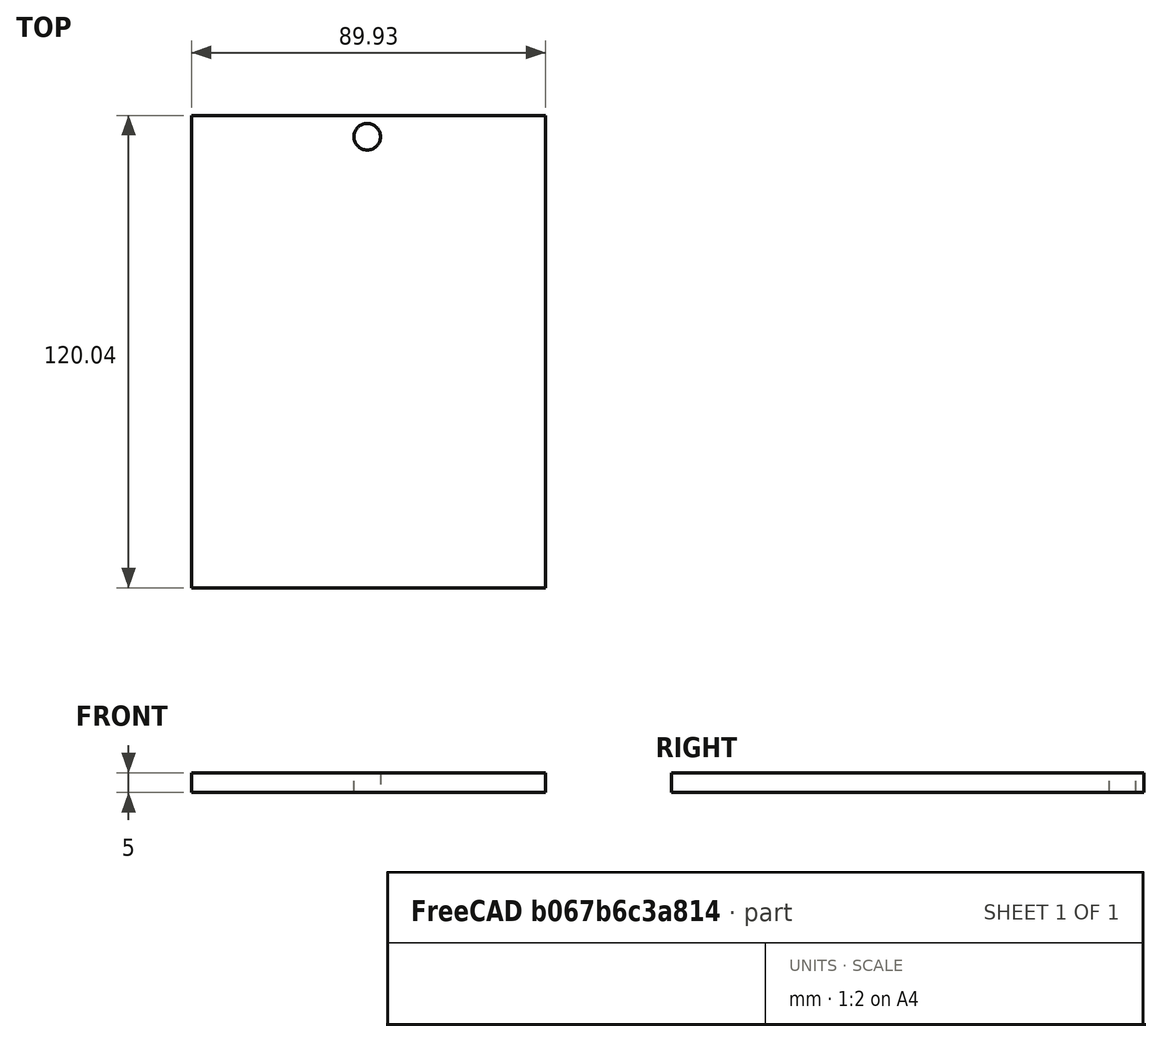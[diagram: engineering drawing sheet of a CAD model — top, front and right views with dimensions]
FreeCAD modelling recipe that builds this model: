
FCSTD DOCUMENT  (FreeCAD 0.14R3702 (Git))
Label: escarrilla
License: CC-BY 3.0
LicenseURL: http://creativecommons.org/licenses/by/3.0/
objects: Sketcher::SketchObject×2, Mesh::Feature×1, PartDesign::Pad×1, PartDesign::Pocket×1
note: 6 computed .brp shape members not serialized (recipe doc carries the construction recipe); baked Part::Feature solids carry a one-line shape summary decoded from their .brp

FEATURE [Mesh::Feature] escarrilla
  Placement = pos=(-64,-50,0) rot=(0,0,1;0rad)
FEATURE [Sketcher::SketchObject] Sketch001
  sketch-geometry (4):
    g0: LineSegment StartX=-9.69851 StartY=109.858 StartZ=0 EndX=80.2331 EndY=109.858 EndZ=0
    g1: LineSegment StartX=80.2331 StartY=109.858 StartZ=0 EndX=80.2331 EndY=-10.1794 EndZ=0
    g2: LineSegment StartX=80.2331 StartY=-10.1794 StartZ=0 EndX=-9.69851 EndY=-10.1794 EndZ=0
    g3: LineSegment StartX=-9.69851 StartY=-10.1794 StartZ=0 EndX=-9.69851 EndY=109.858 EndZ=0
  constraints (8):
    c: Coincident(g0,g1)
    c: Coincident(g1,g2)
    c: Coincident(g2,g3)
    c: Coincident(g3,g0)
    c: Horizontal(g0)
    c: Horizontal(g2)
    c: Vertical(g1)
    c: Vertical(g3)
FEATURE [PartDesign::Pad] Pad
  Length = 5
  Length2 = 100
  Sketch = -> Sketch001
  Type = 0
FEATURE [Sketcher::SketchObject] Sketch
  Placement = pos=(0,0,5) rot=(0,0,1;0rad)
  Support = -> Pad [Face6]
  sketch-geometry (1):
    g0: Circle CenterX=34.95 CenterY=104.419 CenterZ=0 NormalX=0 NormalY=0 NormalZ=1 Radius=3.38
FEATURE [PartDesign::Pocket] Pocket
  Length = 5
  Sketch = -> Sketch
  Type = 0
